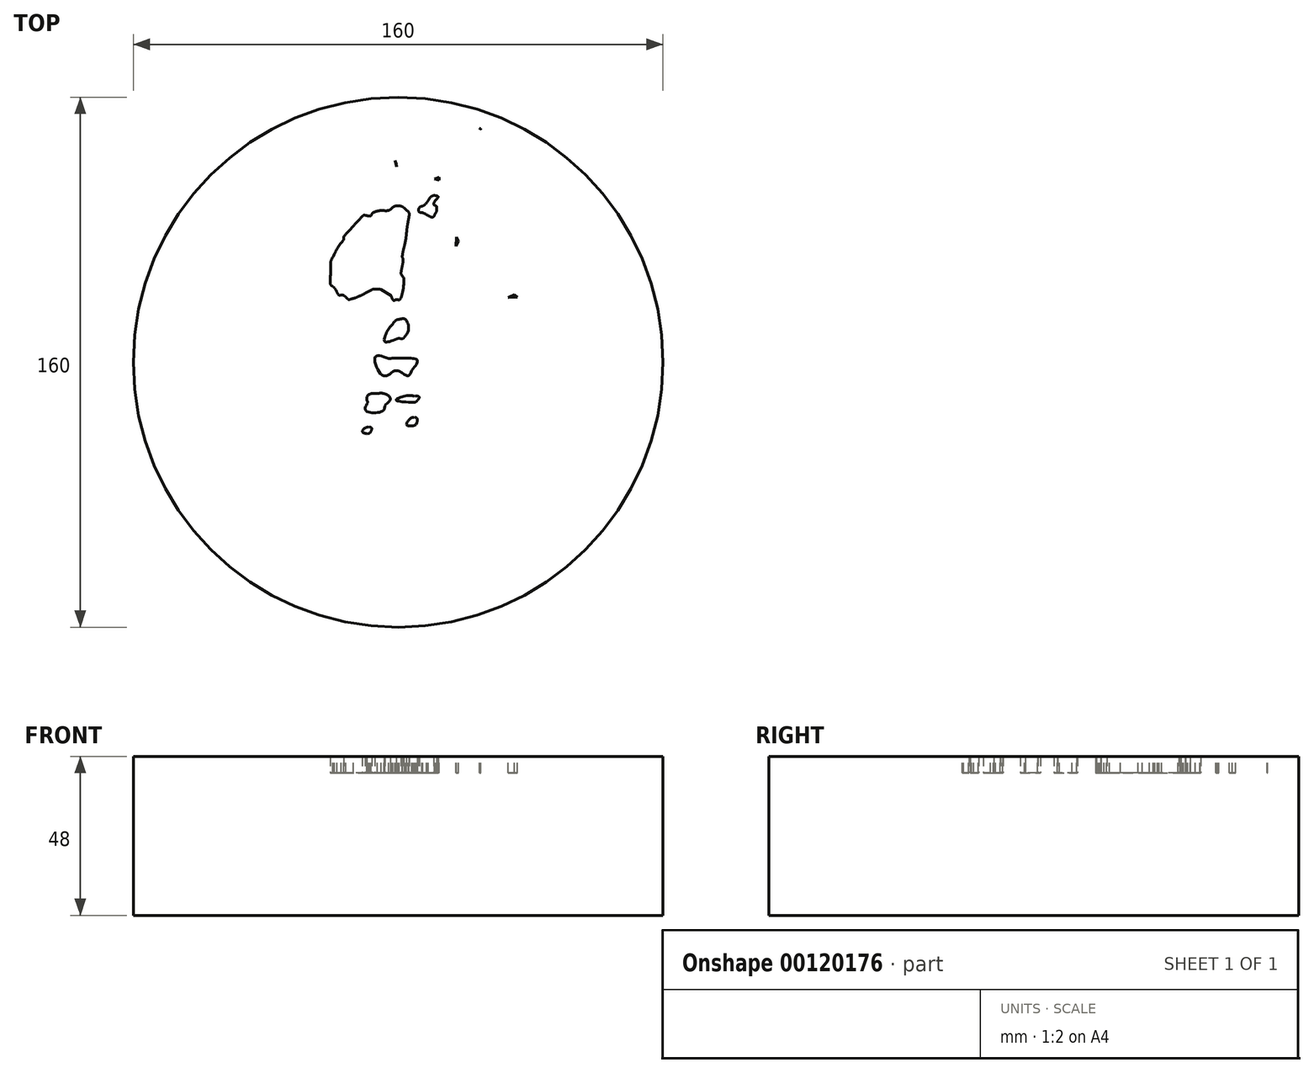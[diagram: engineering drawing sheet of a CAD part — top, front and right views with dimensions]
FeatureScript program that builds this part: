
annotation { "Feature Type Name" : "Feature", "Feature Type Description" : "" }
export const myFeature = defineFeature(function(context is Context, id is Id, definition is map)
    precondition{}
    {
        {
            var Q0;
            Q0=qCreatedBy(makeId("Top.planeOp"),FACE);
            var sketch = newSketch(context, id + "F0", { "sketchPlane" : qUnion([Q0])});
            skCircle(sketch, "E0", {"center": v(0, 0) * mm, "radius": 80 * mm});
            skSolve(sketch);
        }
        {
            var Q0;
            Q0 = qSketchRegion(id + "F0", true);
            extrude(context, id + "F1", {"entities" : qUnion([Q0]), "depth" : 48 * mm});
        }
        {
            var Q0;
            Q0=makeQuery(id+"F1.opExtrude","CAP_FACE",FACE,{"disambiguationData":[OSD([sQuery(id+"F0.wireOp",EDGE,"E0")])],"isStart":false});
            var sketch = newSketch(context, id + "F2", { "sketchPlane" : qUnion([Q0])});
            skFitSpline(sketch, "E1", {"points": [v(23.9, 70.72) * mm, v(23.7, 70.72) * mm, v(23.45, 70.7) * mm, v(22.97, 70.7) * mm]});
            skFitSpline(sketch, "E2", {"points": [v(22.97, 70.7) * mm, v(22.18, 70.72) * mm, v(21.25, 70.78) * mm, v(20.57, 70.38) * mm]});
            skFitSpline(sketch, "E3", {"points": [v(20.57, 70.38) * mm, v(19.9, 69.97) * mm, v(18.86, 69.22) * mm, v(18.86, 68.8) * mm]});
            skFitSpline(sketch, "E4", {"points": [v(18.86, 68.8) * mm, v(18.86, 68.69) * mm, v(19.34, 68.11) * mm, v(19.83, 67.45) * mm]});
            skFitSpline(sketch, "E5", {"points": [v(19.83, 67.45) * mm, v(21.5, 65.23) * mm, v(22.01, 64.9) * mm, v(22.41, 64.07) * mm]});
            skFitSpline(sketch, "E6", {"points": [v(22.41, 64.07) * mm, v(22.94, 63.51) * mm, v(22.84, 63.93) * mm, v(22.42, 62.97) * mm]});
            skFitSpline(sketch, "E7", {"points": [v(22.42, 62.97) * mm, v(22.16, 62.29) * mm, v(21.89, 62.17) * mm, v(20.75, 62.24) * mm]});
            skFitSpline(sketch, "E8", {"points": [v(20.75, 62.24) * mm, v(20, 62.28) * mm, v(19.03, 62.5) * mm, v(18.59, 62.74) * mm]});
            skFitSpline(sketch, "E9", {"points": [v(18.59, 62.74) * mm, v(18.1, 63) * mm, v(17.67, 63.03) * mm, v(17.5, 62.83) * mm]});
            skFitSpline(sketch, "E10", {"points": [v(17.5, 62.83) * mm, v(17.04, 62.33) * mm, v(16.38, 60.17) * mm, v(16.58, 59.85) * mm]});
            skFitSpline(sketch, "E11", {"points": [v(16.58, 59.85) * mm, v(16.68, 59.69) * mm, v(16.42, 59.45) * mm, v(16.02, 59.33) * mm]});
            skFitSpline(sketch, "E12", {"points": [v(16.02, 59.33) * mm, v(15.22, 59.07) * mm, v(12.6, 60.64) * mm, v(12.23, 61.6) * mm]});
            skFitSpline(sketch, "E13", {"points": [v(12.23, 61.6) * mm, v(11.95, 62.32) * mm, v(10.33, 63.72) * mm, v(9.75, 63.73) * mm]});
            skFitSpline(sketch, "E14", {"points": [v(9.75, 63.73) * mm, v(9.5, 63.74) * mm, v(7.43, 64.17) * mm, v(7.65, 64.94) * mm]});
            skFitSpline(sketch, "E15", {"points": [v(7.65, 64.94) * mm, v(8.28, 65.73) * mm, v(9.85, 64.96) * mm, v(10.98, 64.89) * mm]});
            skFitSpline(sketch, "E16", {"points": [v(10.98, 64.89) * mm, v(12.58, 64.79) * mm, v(13.07, 65.17) * mm, v(13.56, 66.88) * mm]});
            skFitSpline(sketch, "E17", {"points": [v(13.56, 66.88) * mm, v(13.92, 68.13) * mm, v(13.36, 68.64) * mm, v(11.8, 68.5) * mm]});
            skFitSpline(sketch, "E18", {"points": [v(11.8, 68.5) * mm, v(11.32, 68.47) * mm, v(10.85, 68.8) * mm, v(10.53, 68.98) * mm]});
            skFitSpline(sketch, "E19", {"points": [v(10.53, 68.98) * mm, v(9.88, 69.32) * mm, v(9.92, 69.46) * mm, v(8.6, 69.06) * mm]});
            skFitSpline(sketch, "E20", {"points": [v(8.6, 69.06) * mm, v(7.5, 68.74) * mm, v(7.03, 68.72) * mm, v(6.94, 69) * mm]});
            skFitSpline(sketch, "E21", {"points": [v(6.94, 69) * mm, v(6.87, 69.2) * mm, v(5.72, 69.1) * mm, v(4.97, 69.1) * mm]});
            skFitSpline(sketch, "E22", {"points": [v(4.97, 69.1) * mm, v(3.34, 69.1) * mm, v(1.85, 67.95) * mm, v(2.16, 66.99) * mm]});
            skFitSpline(sketch, "E23", {"points": [v(2.16, 66.99) * mm, v(2.64, 65.5) * mm, v(3.56, 64.36) * mm, v(3.7, 64.1) * mm]});
            skFitSpline(sketch, "E24", {"points": [v(4.06, 63.48) * mm, v(4.24, 63.16) * mm, v(4.67, 62.57) * mm, v(5.52, 62.15) * mm]});
            skFitSpline(sketch, "E25", {"points": [v(5.52, 62.15) * mm, v(7.27, 61.3) * mm, v(7.33, 60.85) * mm, v(5.77, 60.39) * mm]});
            skFitSpline(sketch, "E26", {"points": [v(5.77, 60.39) * mm, v(3.3, 59.66) * mm, v(3.12, 58.93) * mm, v(4.75, 56.28) * mm]});
            skFitSpline(sketch, "E27", {"points": [v(4.75, 56.28) * mm, v(5.33, 55.33) * mm, v(5.8, 54.32) * mm, v(5.8, 54.03) * mm]});
            skFitSpline(sketch, "E28", {"points": [v(5.8, 54.03) * mm, v(5.8, 53.21) * mm, v(4.89, 53.42) * mm, v(4.25, 54.4) * mm]});
            skFitSpline(sketch, "E29", {"points": [v(4.25, 54.4) * mm, v(3.74, 55.18) * mm, v(3.44, 55.27) * mm, v(1.4, 55.27) * mm]});
            skFitSpline(sketch, "E30", {"points": [v(1.4, 55.27) * mm, v(0.16, 55.27) * mm, v(-1.27, 55.09) * mm, v(-1.76, 54.86) * mm]});
            skFitSpline(sketch, "E31", {"points": [v(-1.76, 54.86) * mm, v(-3, 54.3) * mm, v(-3.3, 54.75) * mm, v(-2.36, 55.75) * mm]});
            skFitSpline(sketch, "E32", {"points": [v(-2.36, 55.75) * mm, v(-1.93, 56.2) * mm, v(-1.69, 57.02) * mm, v(-1.42, 57.4) * mm]});
            skFitSpline(sketch, "E33", {"points": [v(-1.42, 57.4) * mm, v(-1.03, 57.94) * mm, v(-0.47, 58.41) * mm, v(-0.48, 59.04) * mm]});
            skLineSegment(sketch, "E34", {"start": v(3.7, 64.1) * mm, "end": v(4.06, 63.48) * mm});
            skLineSegment(sketch, "E35", {"start": v(4.06, 63.48) * mm, "end": v(3.7, 64.1) * mm});
            skFitSpline(sketch, "E36", {"points": [v(-1, 60.95) * mm, v(-2, 61.77) * mm, v(-1.6, 62.77) * mm, v(-2.27, 63.24) * mm]});
            skFitSpline(sketch, "E37", {"points": [v(-2.27, 63.24) * mm, v(-3.1, 63.8) * mm, v(-5.09, 62.73) * mm, v(-5.28, 63) * mm]});
            skFitSpline(sketch, "E38", {"points": [v(-5.28, 63) * mm, v(-5.4, 63.19) * mm, v(-5.3, 63.47) * mm, v(-5.05, 63.63) * mm]});
            skFitSpline(sketch, "E39", {"points": [v(-5.05, 63.63) * mm, v(-4.48, 64) * mm, v(-3.87, 65.25) * mm, v(-3.32, 67.2) * mm]});
            skFitSpline(sketch, "E40", {"points": [v(-3.32, 67.2) * mm, v(-2.95, 68.5) * mm, v(-2.97, 68.8) * mm, v(-3.45, 69.27) * mm]});
            skFitSpline(sketch, "E41", {"points": [v(-3.45, 69.27) * mm, v(-3.76, 69.58) * mm, v(-4.38, 69.83) * mm, v(-4.83, 69.83) * mm]});
            skFitSpline(sketch, "E42", {"points": [v(-4.83, 69.83) * mm, v(-5.87, 69.83) * mm, v(-12.56, 66.55) * mm, v(-12.8, 65.93) * mm]});
            skFitSpline(sketch, "E43", {"points": [v(-12.8, 65.93) * mm, v(-13.1, 65.14) * mm, v(-11.77, 64.41) * mm, v(-10.33, 64.58) * mm]});
            skFitSpline(sketch, "E44", {"points": [v(-10.33, 64.58) * mm, v(-9.16, 64.71) * mm, v(-7.35, 64.9) * mm, v(-8.09, 64.19) * mm]});
            skFitSpline(sketch, "E45", {"points": [v(-8.09, 64.19) * mm, v(-8.45, 63.83) * mm, v(-10.77, 60.58) * mm, v(-10.77, 59.7) * mm]});
            skFitSpline(sketch, "E46", {"points": [v(-10.77, 59.7) * mm, v(-10.77, 58.63) * mm, v(-10.24, 58.3) * mm, v(-8.72, 58.4) * mm]});
            skFitSpline(sketch, "E47", {"points": [v(-8.72, 58.4) * mm, v(-7.83, 58.46) * mm, v(-6.58, 58.53) * mm, v(-5.65, 58.55) * mm]});
            skFitSpline(sketch, "E48", {"points": [v(-5.65, 58.55) * mm, v(-3.89, 58.59) * mm, v(-5.65, 57.2) * mm, v(-5.84, 56.66) * mm]});
            skLineSegment(sketch, "E49", {"start": v(-0.48, 59.04) * mm, "end": v(-0.5, 59.95) * mm});
            skLineSegment(sketch, "E50", {"start": v(-0.5, 59.95) * mm, "end": v(-1, 60.95) * mm});
            skLineSegment(sketch, "E51", {"start": v(-1, 60.95) * mm, "end": v(-0.48, 59.04) * mm});
            skFitSpline(sketch, "E52", {"points": [v(-6.67, 55.34) * mm, v(-7.13, 54.62) * mm, v(-7.75, 53.82) * mm, v(-8.06, 53.57) * mm]});
            skFitSpline(sketch, "E53", {"points": [v(-8.06, 53.57) * mm, v(-8.66, 53.07) * mm, v(-8.52, 52.3) * mm, v(-7.66, 51.3) * mm]});
            skFitSpline(sketch, "E54", {"points": [v(-7.66, 51.3) * mm, v(-7.2, 50.77) * mm, v(-6.78, 50.7) * mm, v(-5.06, 50.9) * mm]});
            skFitSpline(sketch, "E55", {"points": [v(-5.06, 50.9) * mm, v(-2.63, 51.18) * mm, v(-2.44, 50.8) * mm, v(-4.3, 49.4) * mm]});
            skFitSpline(sketch, "E56", {"points": [v(-4.3, 49.4) * mm, v(-5.28, 48.64) * mm, v(-6, 48.4) * mm, v(-7.43, 48.36) * mm]});
            skFitSpline(sketch, "E57", {"points": [v(-7.43, 48.36) * mm, v(-9.27, 48.3) * mm, v(-10.48, 47.64) * mm, v(-13.86, 44.82) * mm]});
            skFitSpline(sketch, "E58", {"points": [v(-13.86, 44.82) * mm, v(-14.3, 44.46) * mm, v(-15.36, 43.6) * mm, v(-16.24, 42.93) * mm]});
            skFitSpline(sketch, "E59", {"points": [v(-16.24, 42.93) * mm, v(-17.11, 42.25) * mm, v(-17.83, 41.52) * mm, v(-17.83, 41.3) * mm]});
            skFitSpline(sketch, "E60", {"points": [v(-17.83, 41.3) * mm, v(-17.83, 41.09) * mm, v(-18.36, 40.21) * mm, v(-19.01, 39.36) * mm]});
            skFitSpline(sketch, "E61", {"points": [v(-19.01, 39.36) * mm, v(-20.45, 37.47) * mm, v(-21.54, 35.38) * mm, v(-21.87, 33.85) * mm]});
            skFitSpline(sketch, "E62", {"points": [v(-21.87, 33.85) * mm, v(-22, 33.22) * mm, v(-22.26, 32.61) * mm, v(-22.44, 32.5) * mm]});
            skFitSpline(sketch, "E63", {"points": [v(-22.44, 32.5) * mm, v(-22.62, 32.4) * mm, v(-22.77, 31.99) * mm, v(-22.77, 31.6) * mm]});
            skFitSpline(sketch, "E64", {"points": [v(-22.77, 31.6) * mm, v(-22.77, 31.21) * mm, v(-23, 30.44) * mm, v(-23.29, 29.89) * mm]});
            skFitSpline(sketch, "E65", {"points": [v(-23.29, 29.89) * mm, v(-24.54, 27.46) * mm, v(-24.12, 23.5) * mm, v(-22.3, 20.61) * mm]});
            skFitSpline(sketch, "E66", {"points": [v(-22.3, 20.61) * mm, v(-21.71, 19.7) * mm, v(-21.13, 18.94) * mm, v(-21, 18.94) * mm]});
            skFitSpline(sketch, "E67", {"points": [v(-21, 18.94) * mm, v(-20.88, 18.94) * mm, v(-20.24, 18.46) * mm, v(-19.6, 17.88) * mm]});
            skFitSpline(sketch, "E68", {"points": [v(-19.6, 17.88) * mm, v(-18.94, 17.3) * mm, v(-18.13, 16.82) * mm, v(-17.79, 16.82) * mm]});
            skFitSpline(sketch, "E69", {"points": [v(-17.79, 16.82) * mm, v(-17.44, 16.82) * mm, v(-17.07, 16.66) * mm, v(-16.95, 16.47) * mm]});
            skFitSpline(sketch, "E70", {"points": [v(-16.95, 16.47) * mm, v(-16.65, 15.99) * mm, v(-11.23, 16.01) * mm, v(-10.93, 16.5) * mm]});
            skFitSpline(sketch, "E71", {"points": [v(-10.93, 16.5) * mm, v(-10.8, 16.7) * mm, v(-9.85, 17.42) * mm, v(-8.8, 18.09) * mm]});
            skFitSpline(sketch, "E72", {"points": [v(-8.8, 18.09) * mm, v(-5.96, 19.9) * mm, v(-5.07, 19.66) * mm, v(-6.05, 17.3) * mm]});
            skFitSpline(sketch, "E73", {"points": [v(-6.05, 17.3) * mm, v(-6.57, 16.05) * mm, v(-6.57, 15.88) * mm, v(-6, 14.8) * mm]});
            skLineSegment(sketch, "E74", {"start": v(-5.84, 56.66) * mm, "end": v(-6.67, 55.34) * mm});
            skLineSegment(sketch, "E75", {"start": v(-6.67, 55.34) * mm, "end": v(-5.84, 56.66) * mm});
            skFitSpline(sketch, "E76", {"points": [v(-5.39, 13.68) * mm, v(-5.28, 12.38) * mm, v(-4.98, 11.39) * mm, v(-5.3, 10.44) * mm]});
            skFitSpline(sketch, "E77", {"points": [v(-5.3, 10.44) * mm, v(-4.92, 6.56) * mm, v(-6.78, 3.05) * mm, v(-8.22, -0.42) * mm]});
            skFitSpline(sketch, "E78", {"points": [v(-8.22, -0.42) * mm, v(-9.52, -3.6) * mm, v(-10.26, -7.02) * mm, v(-11.35, -10.21) * mm]});
            skFitSpline(sketch, "E79", {"points": [v(-11.35, -10.21) * mm, v(-11.76, -13.4) * mm, v(-12.5, -16.53) * mm, v(-13.6, -19.56) * mm]});
            skFitSpline(sketch, "E80", {"points": [v(-13.6, -19.56) * mm, v(-12.29, -22.65) * mm, v(-10.4, -25.55) * mm, v(-9.64, -28.84) * mm]});
            skFitSpline(sketch, "E81", {"points": [v(-9.64, -28.84) * mm, v(-9.6, -32.33) * mm, v(-8.56, -35.7) * mm, v(-8.66, -39.2) * mm]});
            skFitSpline(sketch, "E82", {"points": [v(-8.66, -39.2) * mm, v(-7.14, -45.43) * mm, v(-7.6, -51.93) * mm, v(-7.18, -58.3) * mm]});
            skFitSpline(sketch, "E83", {"points": [v(-7.18, -58.3) * mm, v(-6.55, -63.17) * mm, v(-12.4, -62.24) * mm, v(-15.18, -63.73) * mm]});
            skFitSpline(sketch, "E84", {"points": [v(-15.18, -63.73) * mm, v(-18.35, -65.08) * mm, v(-21.94, -64.68) * mm, v(-24.8, -61.78) * mm]});
            skFitSpline(sketch, "E85", {"points": [v(-24.8, -61.78) * mm, v(-26.69, -59.87) * mm, v(-27.55, -62.67) * mm, v(-26.8, -64.28) * mm]});
            skFitSpline(sketch, "E86", {"points": [v(-26.8, -64.28) * mm, v(-27.92, -64.34) * mm, v(-29.65, -63.82) * mm, v(-30.85, -64.1) * mm]});
            skFitSpline(sketch, "E87", {"points": [v(-30.85, -64.1) * mm, v(-30.95, -65.2) * mm, v(-29.3, -65.92) * mm, v(-28.86, -66.78) * mm]});
            skFitSpline(sketch, "E88", {"points": [v(-28.86, -66.78) * mm, v(-29.51, -67.36) * mm, v(-31.13, -68.2) * mm, v(-31.03, -69) * mm]});
            skFitSpline(sketch, "E89", {"points": [v(-31.03, -69) * mm, v(-30.94, -69.63) * mm, v(-29.69, -70.08) * mm, v(-28.88, -70.48) * mm]});
            skFitSpline(sketch, "E90", {"points": [v(-28.88, -70.48) * mm, v(-27.89, -70.98) * mm, v(-24.25, -70.62) * mm, v(-20.84, -70.23) * mm]});
            skFitSpline(sketch, "E91", {"points": [v(-20.84, -70.23) * mm, v(-17.2, -69.82) * mm, v(-14.59, -70.82) * mm, v(-11.19, -68.77) * mm]});
            skFitSpline(sketch, "E92", {"points": [v(-11.19, -68.77) * mm, v(-8.34, -67.05) * mm, v(-3.3, -67.46) * mm, v(-2.78, -63.46) * mm]});
            skFitSpline(sketch, "E93", {"points": [v(-2.78, -63.46) * mm, v(-3.8, -60.02) * mm, v(-3.69, -56.22) * mm, v(-5.35, -53) * mm]});
            skFitSpline(sketch, "E94", {"points": [v(-5.35, -53) * mm, v(-4.77, -48.66) * mm, v(-4.45, -44.23) * mm, v(-5.27, -39.9) * mm]});
            skFitSpline(sketch, "E95", {"points": [v(-5.27, -39.9) * mm, v(-7.08, -35.92) * mm, v(-6.64, -31.42) * mm, v(-7.08, -27.18) * mm]});
            skFitSpline(sketch, "E96", {"points": [v(-7.08, -27.18) * mm, v(-7.08, -25.87) * mm, v(-7.81, -24.34) * mm, v(-6.5, -23.44) * mm]});
            skFitSpline(sketch, "E97", {"points": [v(-6.5, -23.44) * mm, v(-3.66, -21.44) * mm, v(-4.72, -17.07) * mm, v(-1.7, -15.5) * mm]});
            skFitSpline(sketch, "E98", {"points": [v(-1.7, -15.5) * mm, v(0.75, -17.58) * mm, v(2.51, -20.76) * mm, v(4.99, -23.1) * mm]});
            skFitSpline(sketch, "E99", {"points": [v(4.99, -23.1) * mm, v(4.47, -25.89) * mm, v(7.27, -27.84) * mm, v(6.25, -30.43) * mm]});
            skFitSpline(sketch, "E100", {"points": [v(6.25, -30.43) * mm, v(7.8, -34.18) * mm, v(6.08, -38.12) * mm, v(6.86, -42.05) * mm]});
            skFitSpline(sketch, "E101", {"points": [v(6.86, -42.05) * mm, v(7.27, -46.6) * mm, v(5.98, -50.97) * mm, v(5.68, -55.46) * mm]});
            skFitSpline(sketch, "E102", {"points": [v(5.68, -55.46) * mm, v(5.45, -58.85) * mm, v(3.24, -62.46) * mm, v(4.27, -65.72) * mm]});
            skFitSpline(sketch, "E103", {"points": [v(4.27, -65.72) * mm, v(6.32, -67.7) * mm, v(9.07, -65.7) * mm, v(11.1, -64.67) * mm]});
            skFitSpline(sketch, "E104", {"points": [v(11.1, -64.67) * mm, v(14.3, -62.4) * mm, v(20.28, -57.24) * mm, v(22.6, -54.28) * mm]});
            skFitSpline(sketch, "E105", {"points": [v(22.6, -54.28) * mm, v(29.36, -52.5) * mm, v(26.52, -53.64) * mm, v(29.36, -52.5) * mm]});
            skFitSpline(sketch, "E106", {"points": [v(29.36, -52.5) * mm, v(31.77, -51.53) * mm, v(32.61, -50.24) * mm, v(31.42, -49.6) * mm]});
            skFitSpline(sketch, "E107", {"points": [v(31.42, -49.6) * mm, v(30.25, -48.96) * mm, v(27.26, -49.63) * mm, v(25.78, -49.23) * mm]});
            skFitSpline(sketch, "E108", {"points": [v(25.78, -49.23) * mm, v(27.4, -46.88) * mm, v(32.18, -45.66) * mm, v(30.39, -43.4) * mm]});
            skFitSpline(sketch, "E109", {"points": [v(30.39, -43.4) * mm, v(28.58, -41.11) * mm, v(25.64, -44.47) * mm, v(24.21, -45.43) * mm]});
            skFitSpline(sketch, "E110", {"points": [v(24.21, -45.43) * mm, v(24.1, -44.26) * mm, v(25.21, -41.72) * mm, v(23.4, -41.66) * mm]});
            skFitSpline(sketch, "E111", {"points": [v(23.4, -41.66) * mm, v(21.66, -41.6) * mm, v(21.36, -47.49) * mm, v(20.5, -49.07) * mm]});
            skFitSpline(sketch, "E112", {"points": [v(20.5, -49.07) * mm, v(17.43, -51.02) * mm, v(15.19, -54.1) * mm, v(12.84, -56.9) * mm]});
            skFitSpline(sketch, "E113", {"points": [v(12.84, -56.9) * mm, v(11.7, -58.88) * mm, v(6.15, -61.65) * mm, v(8.2, -57.15) * mm]});
            skFitSpline(sketch, "E114", {"points": [v(8.2, -57.15) * mm, v(8.86, -52.68) * mm, v(9.03, -48.15) * mm, v(9.53, -43.66) * mm]});
            skFitSpline(sketch, "E115", {"points": [v(9.53, -43.66) * mm, v(9.75, -40.72) * mm, v(9.42, -37.42) * mm, v(8.73, -34.52) * mm]});
            skFitSpline(sketch, "E116", {"points": [v(8.73, -34.52) * mm, v(9.58, -30.47) * mm, v(7.29, -26.7) * mm, v(7.64, -22.7) * mm]});
            skFitSpline(sketch, "E117", {"points": [v(7.64, -22.7) * mm, v(8.74, -18.06) * mm, v(8.9, -13.27) * mm, v(8.49, -8.54) * mm]});
            skFitSpline(sketch, "E118", {"points": [v(8.49, -8.54) * mm, v(8.26, -4.97) * mm, v(6.72, -1.71) * mm, v(6.23, 1.72) * mm]});
            skFitSpline(sketch, "E119", {"points": [v(6.23, 1.72) * mm, v(5.36, 5.56) * mm, v(4.63, 9.9) * mm, v(3.43, 13.67) * mm]});
            skLineSegment(sketch, "E120", {"start": v(-6, 14.8) * mm, "end": v(-5.39, 13.68) * mm});
            skLineSegment(sketch, "E121", {"start": v(-5.39, 13.68) * mm, "end": v(-6, 14.8) * mm});
            skFitSpline(sketch, "E122", {"points": [v(3.2, 15.38) * mm, v(3.07, 16.36) * mm, v(3.11, 17.21) * mm, v(3.3, 17.33) * mm]});
            skFitSpline(sketch, "E123", {"points": [v(3.3, 17.33) * mm, v(3.48, 17.44) * mm, v(3.62, 18.68) * mm, v(3.61, 20.09) * mm]});
            skFitSpline(sketch, "E124", {"points": [v(3.61, 20.09) * mm, v(3.6, 21.5) * mm, v(3.71, 23.83) * mm, v(3.86, 25.29) * mm]});
            skFitSpline(sketch, "E125", {"points": [v(3.86, 25.29) * mm, v(4, 26.74) * mm, v(4.17, 28.65) * mm, v(4.23, 29.52) * mm]});
            skFitSpline(sketch, "E126", {"points": [v(4.23, 29.52) * mm, v(4.38, 31.69) * mm, v(4.62, 32.94) * mm, v(5.11, 34.13) * mm]});
            skFitSpline(sketch, "E127", {"points": [v(5.11, 34.13) * mm, v(5.34, 34.69) * mm, v(5.55, 35.9) * mm, v(5.58, 36.83) * mm]});
            skFitSpline(sketch, "E128", {"points": [v(5.58, 36.83) * mm, v(5.63, 38.4) * mm, v(5.7, 38.51) * mm, v(6.51, 38.43) * mm]});
            skFitSpline(sketch, "E129", {"points": [v(6.51, 38.43) * mm, v(7, 38.39) * mm, v(8.39, 38.3) * mm, v(9.6, 38.24) * mm]});
            skFitSpline(sketch, "E130", {"points": [v(9.6, 38.24) * mm, v(10.82, 38.17) * mm, v(12, 37.93) * mm, v(12.23, 37.7) * mm]});
            skFitSpline(sketch, "E131", {"points": [v(12.23, 37.7) * mm, v(12.46, 37.47) * mm, v(13.08, 37.28) * mm, v(13.6, 37.28) * mm]});
            skFitSpline(sketch, "E132", {"points": [v(13.6, 37.28) * mm, v(15.14, 37.28) * mm, v(15.43, 35.66) * mm, v(14.28, 33.4) * mm]});
            skFitSpline(sketch, "E133", {"points": [v(14.28, 33.4) * mm, v(13.48, 31.84) * mm, v(13.35, 30.01) * mm, v(14.01, 29.78) * mm]});
            skFitSpline(sketch, "E134", {"points": [v(14.01, 29.78) * mm, v(14.25, 29.7) * mm, v(15.42, 29.7) * mm, v(16.6, 29.8) * mm]});
            skFitSpline(sketch, "E135", {"points": [v(16.6, 29.8) * mm, v(18.93, 29.98) * mm, v(19.5, 29.66) * mm, v(18.88, 28.5) * mm]});
            skFitSpline(sketch, "E136", {"points": [v(18.88, 28.5) * mm, v(18.68, 28.13) * mm, v(18.42, 26.72) * mm, v(18.3, 25.38) * mm]});
            skFitSpline(sketch, "E137", {"points": [v(18.3, 25.38) * mm, v(18.1, 23.38) * mm, v(18.18, 22.76) * mm, v(18.68, 22) * mm]});
            skFitSpline(sketch, "E138", {"points": [v(18.68, 22) * mm, v(19.45, 20.82) * mm, v(20.16, 20.82) * mm, v(22.6, 21.96) * mm]});
            skFitSpline(sketch, "E139", {"points": [v(22.6, 21.96) * mm, v(24, 22.63) * mm, v(24.8, 22.8) * mm, v(25.6, 22.64) * mm]});
            skFitSpline(sketch, "E140", {"points": [v(25.6, 22.64) * mm, v(26.76, 22.38) * mm, v(27.43, 21.24) * mm, v(26.96, 20.33) * mm]});
            skFitSpline(sketch, "E141", {"points": [v(26.96, 20.33) * mm, v(26.5, 19.47) * mm, v(26.82, 17.8) * mm, v(27.54, 17.28) * mm]});
            skFitSpline(sketch, "E142", {"points": [v(27.54, 17.28) * mm, v(28.01, 16.93) * mm, v(29.06, 16.86) * mm, v(31.6, 17) * mm]});
            skFitSpline(sketch, "E143", {"points": [v(31.6, 17) * mm, v(34.44, 17.15) * mm, v(35.04, 17.1) * mm, v(35.21, 16.65) * mm]});
            skFitSpline(sketch, "E144", {"points": [v(35.21, 16.65) * mm, v(35.33, 16.36) * mm, v(35.74, 16.12) * mm, v(36.14, 16.12) * mm]});
            skFitSpline(sketch, "E145", {"points": [v(36.14, 16.12) * mm, v(37.25, 16.12) * mm, v(37.14, 18.54) * mm, v(35.98, 19.63) * mm]});
            skLineSegment(sketch, "E146", {"start": v(3.43, 13.67) * mm, "end": v(3.2, 15.38) * mm});
            skLineSegment(sketch, "E147", {"start": v(3.2, 15.38) * mm, "end": v(3.43, 13.67) * mm});
            skFitSpline(sketch, "E148", {"points": [v(33.22, 19.52) * mm, v(31.18, 18.52) * mm, v(29.99, 18.34) * mm, v(29.6, 18.98) * mm]});
            skFitSpline(sketch, "E149", {"points": [v(29.6, 18.98) * mm, v(29.46, 19.2) * mm, v(29.31, 20.35) * mm, v(29.26, 21.54) * mm]});
            skFitSpline(sketch, "E150", {"points": [v(29.26, 21.54) * mm, v(29.09, 25.98) * mm, v(28.18, 26.74) * mm, v(24.79, 25.3) * mm]});
            skFitSpline(sketch, "E151", {"points": [v(24.79, 25.3) * mm, v(23.5, 24.77) * mm, v(22.09, 24.34) * mm, v(21.63, 24.36) * mm]});
            skFitSpline(sketch, "E152", {"points": [v(21.63, 24.36) * mm, v(20.89, 24.4) * mm, v(20.83, 24.54) * mm, v(20.93, 26) * mm]});
            skFitSpline(sketch, "E153", {"points": [v(20.93, 26) * mm, v(21, 26.87) * mm, v(21.27, 28.12) * mm, v(21.54, 28.77) * mm]});
            skFitSpline(sketch, "E154", {"points": [v(21.54, 28.77) * mm, v(22.24, 30.45) * mm, v(22.16, 31.11) * mm, v(21.15, 32.2) * mm]});
            skFitSpline(sketch, "E155", {"points": [v(21.15, 32.2) * mm, v(20.33, 33.09) * mm, v(20.16, 33.13) * mm, v(19, 32.78) * mm]});
            skFitSpline(sketch, "E156", {"points": [v(19, 32.78) * mm, v(17.73, 32.39) * mm, v(16.74, 32.52) * mm, v(16.74, 33.08) * mm]});
            skFitSpline(sketch, "E157", {"points": [v(16.74, 33.08) * mm, v(16.74, 33.25) * mm, v(17.09, 34.09) * mm, v(17.5, 34.94) * mm]});
            skLineSegment(sketch, "E158", {"start": v(35.98, 19.63) * mm, "end": v(35.12, 20.45) * mm});
            skLineSegment(sketch, "E159", {"start": v(35.12, 20.45) * mm, "end": v(33.22, 19.52) * mm});
            skLineSegment(sketch, "E160", {"start": v(33.22, 19.52) * mm, "end": v(35.98, 19.63) * mm});
            skFitSpline(sketch, "E161", {"points": [v(17.56, 37.86) * mm, v(17.1, 38.77) * mm, v(16.57, 39.26) * mm, v(16, 39.34) * mm]});
            skFitSpline(sketch, "E162", {"points": [v(16, 39.34) * mm, v(14.96, 39.5) * mm, v(14.28, 40.03) * mm, v(14.28, 40.7) * mm]});
            skFitSpline(sketch, "E163", {"points": [v(14.28, 40.7) * mm, v(14.28, 41.4) * mm, v(17.68, 45.41) * mm, v(19.12, 46.4) * mm]});
            skFitSpline(sketch, "E164", {"points": [v(19.12, 46.4) * mm, v(20.24, 47.17) * mm, v(21.63, 47.22) * mm, v(21.17, 46.48) * mm]});
            skFitSpline(sketch, "E165", {"points": [v(21.17, 46.48) * mm, v(21.05, 46.3) * mm, v(20.8, 45.25) * mm, v(20.6, 44.15) * mm]});
            skFitSpline(sketch, "E166", {"points": [v(20.6, 44.15) * mm, v(20.27, 42.42) * mm, v(20.3, 42.06) * mm, v(20.84, 41.48) * mm]});
            skFitSpline(sketch, "E167", {"points": [v(20.84, 41.48) * mm, v(21.6, 40.63) * mm, v(22.08, 40.78) * mm, v(25.04, 42.77) * mm]});
            skFitSpline(sketch, "E168", {"points": [v(25.04, 42.77) * mm, v(26.33, 43.63) * mm, v(27.58, 44.34) * mm, v(27.81, 44.34) * mm]});
            skFitSpline(sketch, "E169", {"points": [v(27.81, 44.34) * mm, v(28.6, 44.34) * mm, v(29.1, 43.5) * mm, v(29.1, 42.15) * mm]});
            skFitSpline(sketch, "E170", {"points": [v(29.1, 42.15) * mm, v(29.1, 39.53) * mm, v(31.57, 38.56) * mm, v(34.04, 40.23) * mm]});
            skFitSpline(sketch, "E171", {"points": [v(34.04, 40.23) * mm, v(36.35, 41.78) * mm, v(38.99, 42.95) * mm, v(39.14, 42.48) * mm]});
            skFitSpline(sketch, "E172", {"points": [v(39.14, 42.48) * mm, v(39.22, 42.24) * mm, v(39.7, 40.77) * mm, v(40.21, 39.22) * mm]});
            skFitSpline(sketch, "E173", {"points": [v(40.21, 39.22) * mm, v(41.54, 35.18) * mm, v(42.44, 34.4) * mm, v(44.17, 35.85) * mm]});
            skFitSpline(sketch, "E174", {"points": [v(44.17, 35.85) * mm, v(45.15, 36.67) * mm, v(45.18, 37.4) * mm, v(44.26, 38.03) * mm]});
            skFitSpline(sketch, "E175", {"points": [v(44.26, 38.03) * mm, v(43.68, 38.43) * mm, v(43.52, 39.07) * mm, v(43.33, 41.61) * mm]});
            skFitSpline(sketch, "E176", {"points": [v(43.33, 41.61) * mm, v(43.07, 45.08) * mm, v(42.5, 46.11) * mm, v(40.76, 46.31) * mm]});
            skFitSpline(sketch, "E177", {"points": [v(40.76, 46.31) * mm, v(39.71, 46.44) * mm, v(36.72, 45.33) * mm, v(36.3, 44.67) * mm]});
            skFitSpline(sketch, "E178", {"points": [v(36.3, 44.67) * mm, v(35.98, 44.14) * mm, v(33.52, 42.65) * mm, v(32.76, 42.51) * mm]});
            skFitSpline(sketch, "E179", {"points": [v(32.76, 42.51) * mm, v(32.2, 42.42) * mm, v(32.11, 42.59) * mm, v(32.2, 43.54) * mm]});
            skFitSpline(sketch, "E180", {"points": [v(32.2, 43.54) * mm, v(32.27, 44.16) * mm, v(32.19, 44.88) * mm, v(32.03, 45.12) * mm]});
            skFitSpline(sketch, "E181", {"points": [v(32.03, 45.12) * mm, v(31.87, 45.37) * mm, v(31.74, 46.29) * mm, v(31.74, 47.16) * mm]});
            skFitSpline(sketch, "E182", {"points": [v(31.74, 47.16) * mm, v(31.74, 48.64) * mm, v(31.67, 48.76) * mm, v(30.75, 48.86) * mm]});
            skFitSpline(sketch, "E183", {"points": [v(30.75, 48.86) * mm, v(30.17, 48.93) * mm, v(29.02, 48.6) * mm, v(28.01, 48.06) * mm]});
            skFitSpline(sketch, "E184", {"points": [v(28.01, 48.06) * mm, v(27.05, 47.56) * mm, v(26.27, 47.25) * mm, v(26.27, 47.38) * mm]});
            skFitSpline(sketch, "E185", {"points": [v(26.27, 47.38) * mm, v(26.27, 47.5) * mm, v(26.06, 47.43) * mm, v(25.8, 47.22) * mm]});
            skFitSpline(sketch, "E186", {"points": [v(25.8, 47.22) * mm, v(25.46, 46.93) * mm, v(25.2, 47.07) * mm, v(24.76, 47.83) * mm]});
            skFitSpline(sketch, "E187", {"points": [v(24.76, 47.83) * mm, v(24.44, 48.38) * mm, v(24.25, 48.9) * mm, v(24.35, 49) * mm]});
            skFitSpline(sketch, "E188", {"points": [v(24.35, 49) * mm, v(24.45, 49.1) * mm, v(24.37, 49.87) * mm, v(24.19, 50.72) * mm]});
            skFitSpline(sketch, "E189", {"points": [v(24.19, 50.72) * mm, v(23.95, 51.78) * mm, v(23.96, 52.4) * mm, v(24.22, 52.71) * mm]});
            skFitSpline(sketch, "E190", {"points": [v(24.22, 52.71) * mm, v(24.85, 53.47) * mm, v(24.4, 53.5) * mm, v(22.9, 52.83) * mm]});
            skFitSpline(sketch, "E191", {"points": [v(22.9, 52.83) * mm, v(22.11, 52.48) * mm, v(21.2, 51.78) * mm, v(20.87, 51.27) * mm]});
            skFitSpline(sketch, "E192", {"points": [v(20.87, 51.27) * mm, v(20.53, 50.75) * mm, v(20.06, 50.33) * mm, v(19.82, 50.33) * mm]});
            skFitSpline(sketch, "E193", {"points": [v(19.82, 50.33) * mm, v(19.43, 50.33) * mm, v(17.44, 48.28) * mm, v(16.27, 46.66) * mm]});
            skFitSpline(sketch, "E194", {"points": [v(16.27, 46.66) * mm, v(16, 46.29) * mm, v(15.56, 46.08) * mm, v(15.27, 46.19) * mm]});
            skFitSpline(sketch, "E195", {"points": [v(15.27, 46.19) * mm, v(14.85, 46.35) * mm, v(14.8, 46.77) * mm, v(15, 48.27) * mm]});
            skFitSpline(sketch, "E196", {"points": [v(15, 48.27) * mm, v(15.3, 50.48) * mm, v(14.84, 53.86) * mm, v(14.2, 54.28) * mm]});
            skFitSpline(sketch, "E197", {"points": [v(14.2, 54.28) * mm, v(13.95, 54.44) * mm, v(13.11, 54.75) * mm, v(12.33, 54.97) * mm]});
            skLineSegment(sketch, "E198", {"start": v(17.5, 34.94) * mm, "end": v(18.26, 36.5) * mm});
            skLineSegment(sketch, "E199", {"start": v(18.26, 36.5) * mm, "end": v(17.56, 37.86) * mm});
            skLineSegment(sketch, "E200", {"start": v(17.56, 37.86) * mm, "end": v(17.5, 34.94) * mm});
            skFitSpline(sketch, "E201", {"points": [v(12.33, 55.86) * mm, v(13.3, 56.21) * mm, v(14.3, 56.29) * mm, v(15.5, 56.1) * mm]});
            skFitSpline(sketch, "E202", {"points": [v(15.5, 56.1) * mm, v(18.02, 55.74) * mm, v(20.56, 55.93) * mm, v(21.83, 56.58) * mm]});
            skFitSpline(sketch, "E203", {"points": [v(21.83, 56.58) * mm, v(22.98, 57.16) * mm, v(23.39, 57.67) * mm, v(23.97, 59.21) * mm]});
            skFitSpline(sketch, "E204", {"points": [v(23.97, 59.21) * mm, v(24.17, 59.73) * mm, v(25.04, 60.7) * mm, v(25.92, 61.35) * mm]});
            skFitSpline(sketch, "E205", {"points": [v(25.92, 61.35) * mm, v(26.84, 62.04) * mm, v(27.55, 62.88) * mm, v(27.62, 63.36) * mm]});
            skFitSpline(sketch, "E206", {"points": [v(27.62, 63.36) * mm, v(27.03, 64.38) * mm, v(26.58, 65.21) * mm, v(25.77, 66.43) * mm]});
            skFitSpline(sketch, "E207", {"points": [v(25.77, 66.43) * mm, v(25.44, 67.3) * mm, v(26.13, 67.88) * mm, v(26.93, 67.38) * mm]});
            skFitSpline(sketch, "E208", {"points": [v(26.93, 67.38) * mm, v(27.46, 67.05) * mm, v(27.65, 67.13) * mm, v(28.1, 67.92) * mm]});
            skFitSpline(sketch, "E209", {"points": [v(28.1, 67.92) * mm, v(28.7, 68.94) * mm, v(28.52, 69.85) * mm, v(27.68, 70.03) * mm]});
            skFitSpline(sketch, "E210", {"points": [v(27.68, 70.03) * mm, v(26.91, 70.18) * mm, v(27.07, 70.14) * mm, v(25.84, 70.46) * mm]});
            skFitSpline(sketch, "E211", {"points": [v(25.84, 70.46) * mm, v(24.52, 70.6) * mm, v(24.97, 70.43) * mm, v(24.52, 70.6) * mm]});
            skFitSpline(sketch, "E212", {"points": [v(24.52, 70.6) * mm, v(24.23, 70.7) * mm, v(24.09, 70.72) * mm, v(23.9, 70.72) * mm]});
            skLineSegment(sketch, "E213", {"start": v(12.33, 54.97) * mm, "end": v(10.92, 55.36) * mm});
            skLineSegment(sketch, "E214", {"start": v(10.92, 55.36) * mm, "end": v(12.33, 55.86) * mm});
            skLineSegment(sketch, "E215", {"start": v(12.33, 55.86) * mm, "end": v(12.33, 54.97) * mm});
            skFitSpline(sketch, "E216", {"points": [v(11.4, 50.27) * mm, v(11.56, 50.26) * mm, v(11.71, 50.22) * mm, v(11.84, 50.13) * mm]});
            skFitSpline(sketch, "E217", {"points": [v(11.84, 50.13) * mm, v(12.07, 50) * mm, v(12.03, 49.7) * mm, v(11.7, 49.33) * mm]});
            skFitSpline(sketch, "E218", {"points": [v(11.7, 49.33) * mm, v(11, 48.5) * mm, v(10.72, 47.57) * mm, v(11.12, 47.33) * mm]});
            skFitSpline(sketch, "E219", {"points": [v(11.12, 47.33) * mm, v(11.56, 47.05) * mm, v(11.55, 45.52) * mm, v(11.09, 44.67) * mm]});
            skFitSpline(sketch, "E220", {"points": [v(11.09, 44.67) * mm, v(10.67, 43.89) * mm, v(9.9, 43.84) * mm, v(8.63, 44.53) * mm]});
            skFitSpline(sketch, "E221", {"points": [v(8.63, 44.53) * mm, v(8.15, 44.8) * mm, v(7.47, 45.09) * mm, v(7.13, 45.19) * mm]});
            skFitSpline(sketch, "E222", {"points": [v(7.13, 45.19) * mm, v(6.23, 45.46) * mm, v(6.38, 46.62) * mm, v(7.39, 47.16) * mm]});
            skFitSpline(sketch, "E223", {"points": [v(7.39, 47.16) * mm, v(7.87, 47.41) * mm, v(8.62, 48.15) * mm, v(9.06, 48.79) * mm]});
            skFitSpline(sketch, "E224", {"points": [v(9.06, 48.79) * mm, v(9.7, 49.72) * mm, v(10.68, 50.31) * mm, v(11.4, 50.27) * mm]});
            skFitSpline(sketch, "E225", {"points": [v(-0.16, 47.16) * mm, v(0.66, 47.17) * mm, v(1.52, 46.81) * mm, v(2.29, 46.1) * mm]});
            skFitSpline(sketch, "E226", {"points": [v(2.29, 46.1) * mm, v(3.34, 45.11) * mm, v(3.4, 44.91) * mm, v(3.18, 43.54) * mm]});
            skFitSpline(sketch, "E227", {"points": [v(3.18, 43.54) * mm, v(2.77, 41.07) * mm, v(2.67, 40.36) * mm, v(2.48, 38.61) * mm]});
            skFitSpline(sketch, "E228", {"points": [v(2.48, 38.61) * mm, v(2.37, 37.7) * mm, v(2.04, 35.82) * mm, v(1.73, 34.45) * mm]});
            skFitSpline(sketch, "E229", {"points": [v(1.73, 34.45) * mm, v(1.41, 33.08) * mm, v(1.26, 31.7) * mm, v(1.37, 31.4) * mm]});
            skFitSpline(sketch, "E230", {"points": [v(1.37, 31.4) * mm, v(1.5, 31.09) * mm, v(1.41, 29.92) * mm, v(1.2, 28.81) * mm]});
            skFitSpline(sketch, "E231", {"points": [v(1.2, 28.81) * mm, v(0.92, 27.44) * mm, v(0.9, 26.58) * mm, v(1.15, 26.13) * mm]});
            skFitSpline(sketch, "E232", {"points": [v(1.15, 26.13) * mm, v(1.7, 25.11) * mm, v(0.54, 18.94) * mm, v(-0.2, 18.94) * mm]});
            skFitSpline(sketch, "E233", {"points": [v(-0.2, 18.94) * mm, v(-0.36, 18.94) * mm, v(-0.71, 18.85) * mm, v(-0.99, 18.74) * mm]});
            skFitSpline(sketch, "E234", {"points": [v(-0.99, 18.74) * mm, v(-1.34, 18.61) * mm, v(-1.72, 19.06) * mm, v(-2.2, 20.19) * mm]});
            skFitSpline(sketch, "E235", {"points": [v(-5.19, 21.98) * mm, v(-7.25, 22.12) * mm, v(-7.68, 22.02) * mm, v(-9.82, 20.9) * mm]});
            skFitSpline(sketch, "E236", {"points": [v(-9.82, 20.9) * mm, v(-11.12, 20.23) * mm, v(-12.8, 19.49) * mm, v(-13.56, 19.26) * mm]});
            skFitSpline(sketch, "E237", {"points": [v(-13.56, 19.26) * mm, v(-14.8, 18.89) * mm, v(-15.02, 18.92) * mm, v(-15.75, 19.6) * mm]});
            skFitSpline(sketch, "E238", {"points": [v(-15.75, 19.6) * mm, v(-16.2, 20.03) * mm, v(-16.88, 20.32) * mm, v(-17.27, 20.27) * mm]});
            skFitSpline(sketch, "E239", {"points": [v(-17.27, 20.27) * mm, v(-17.74, 20.2) * mm, v(-18.15, 20.51) * mm, v(-18.52, 21.22) * mm]});
            skFitSpline(sketch, "E240", {"points": [v(-18.52, 21.22) * mm, v(-18.82, 21.79) * mm, v(-19.38, 22.53) * mm, v(-19.77, 22.86) * mm]});
            skFitSpline(sketch, "E241", {"points": [v(-19.77, 22.86) * mm, v(-20.4, 23.4) * mm, v(-20.47, 23.87) * mm, v(-20.43, 26.94) * mm]});
            skFitSpline(sketch, "E242", {"points": [v(-20.43, 26.94) * mm, v(-20.4, 30.15) * mm, v(-20.3, 30.6) * mm, v(-19.22, 32.7) * mm]});
            skFitSpline(sketch, "E243", {"points": [v(-19.22, 32.7) * mm, v(-18.58, 33.96) * mm, v(-17.68, 35.44) * mm, v(-17.23, 35.99) * mm]});
            skFitSpline(sketch, "E244", {"points": [v(-17.23, 35.99) * mm, v(-16.78, 36.54) * mm, v(-16.42, 37.15) * mm, v(-16.42, 37.36) * mm]});
            skFitSpline(sketch, "E245", {"points": [v(-16.42, 37.36) * mm, v(-16.42, 37.77) * mm, v(-14.75, 39.8) * mm, v(-12.1, 42.64) * mm]});
            skFitSpline(sketch, "E246", {"points": [v(-12.1, 42.64) * mm, v(-10.63, 44.21) * mm, v(-10.3, 44.4) * mm, v(-9.38, 44.22) * mm]});
            skFitSpline(sketch, "E247", {"points": [v(-9.38, 44.22) * mm, v(-8.8, 44.1) * mm, v(-8.24, 44.15) * mm, v(-8.13, 44.33) * mm]});
            skFitSpline(sketch, "E248", {"points": [v(-8.13, 44.33) * mm, v(-7.72, 45) * mm, v(-5.66, 45.75) * mm, v(-4.25, 45.75) * mm]});
            skFitSpline(sketch, "E249", {"points": [v(-4.25, 45.75) * mm, v(-3.27, 45.75) * mm, v(-2.49, 46) * mm, v(-1.95, 46.45) * mm]});
            skFitSpline(sketch, "E250", {"points": [v(-1.95, 46.45) * mm, v(-1.42, 46.92) * mm, v(-0.8, 47.15) * mm, v(-0.16, 47.16) * mm]});
            skLineSegment(sketch, "E251", {"start": v(-2.2, 20.19) * mm, "end": v(-2.91, 21.82) * mm});
            skLineSegment(sketch, "E252", {"start": v(-2.91, 21.82) * mm, "end": v(-5.19, 21.98) * mm});
            skLineSegment(sketch, "E253", {"start": v(-5.19, 21.98) * mm, "end": v(-2.2, 20.19) * mm});
            skFitSpline(sketch, "E254", {"points": [v(-4.72, 43.17) * mm, v(-4.85, 43.17) * mm, v(-4.97, 43.15) * mm, v(-5.08, 43.12) * mm]});
            skFitSpline(sketch, "E255", {"points": [v(-5.08, 43.12) * mm, v(-5.84, 42.88) * mm, v(-7, 41.16) * mm, v(-7.35, 39.71) * mm]});
            skFitSpline(sketch, "E256", {"points": [v(-7.35, 39.71) * mm, v(-7.48, 39.22) * mm, v(-8.14, 38.11) * mm, v(-8.82, 37.25) * mm]});
            skFitSpline(sketch, "E257", {"points": [v(-8.82, 37.25) * mm, v(-9.5, 36.4) * mm, v(-10.06, 35.58) * mm, v(-10.06, 35.45) * mm]});
            skFitSpline(sketch, "E258", {"points": [v(-10.06, 35.45) * mm, v(-10.07, 34.97) * mm, v(-12.28, 31.93) * mm, v(-12.76, 31.75) * mm]});
            skFitSpline(sketch, "E259", {"points": [v(-12.76, 31.75) * mm, v(-13.5, 31.46) * mm, v(-13.33, 30.6) * mm, v(-12.45, 30.23) * mm]});
            skFitSpline(sketch, "E260", {"points": [v(-12.45, 30.23) * mm, v(-11.84, 29.99) * mm, v(-9.74, 30.07) * mm, v(-9.5, 30.36) * mm]});
            skFitSpline(sketch, "E261", {"points": [v(-9.5, 30.36) * mm, v(-9.47, 30.38) * mm, v(-9.03, 31.09) * mm, v(-8.5, 31.93) * mm]});
            skFitSpline(sketch, "E262", {"points": [v(-8.5, 31.93) * mm, v(-7.54, 33.49) * mm, v(-6.65, 33.73) * mm, v(-6.8, 32.4) * mm]});
            skFitSpline(sketch, "E263", {"points": [v(-6.8, 32.4) * mm, v(-6.91, 31.37) * mm, v(-4.92, 30.37) * mm, v(-3.12, 30.54) * mm]});
            skFitSpline(sketch, "E264", {"points": [v(-3.12, 30.54) * mm, v(-2.44, 30.6) * mm, v(-0.96, 32.13) * mm, v(-0.57, 33.16) * mm]});
            skFitSpline(sketch, "E265", {"points": [v(-0.57, 33.16) * mm, v(0.08, 34.86) * mm, v(-0.87, 36.3) * mm, v(-2.92, 36.74) * mm]});
            skFitSpline(sketch, "E266", {"points": [v(-2.92, 36.74) * mm, v(-3.87, 36.94) * mm, v(-4.07, 37.15) * mm, v(-4.06, 37.93) * mm]});
            skFitSpline(sketch, "E267", {"points": [v(-4.06, 37.93) * mm, v(-4.05, 38.45) * mm, v(-3.66, 39.5) * mm, v(-3.18, 40.28) * mm]});
            skFitSpline(sketch, "E268", {"points": [v(-3.18, 40.28) * mm, v(-2.7, 41.06) * mm, v(-2.3, 41.87) * mm, v(-2.3, 42.1) * mm]});
            skFitSpline(sketch, "E269", {"points": [v(-2.3, 42.1) * mm, v(-2.3, 42.6) * mm, v(-3.79, 43.2) * mm, v(-4.72, 43.17) * mm]});
            skFitSpline(sketch, "E270", {"points": [v(0.31, 12.87) * mm, v(2.09, 12.97) * mm, v(3.16, 9.81) * mm, v(1.97, 7.7) * mm]});
            skFitSpline(sketch, "E271", {"points": [v(1.97, 7.7) * mm, v(1.37, 7.12) * mm, v(0.42, 7.17) * mm, v(-0.35, 7.08) * mm]});
            skFitSpline(sketch, "E272", {"points": [v(-0.35, 7.08) * mm, v(-4.1, 6.3) * mm, v(-3.05, 9.73) * mm, v(-1.64, 11.52) * mm]});
            skFitSpline(sketch, "E273", {"points": [v(-1.64, 11.52) * mm, v(-0.95, 12.44) * mm, v(-0.28, 12.84) * mm, v(0.31, 12.87) * mm]});
            skFitSpline(sketch, "E274", {"points": [v(-0.44, 1.2) * mm, v(2.39, 1.18) * mm, v(5.75, 0.65) * mm, v(4.18, -2.42) * mm]});
            skFitSpline(sketch, "E275", {"points": [v(4.18, -2.42) * mm, v(2.9, -4.1) * mm, v(0.21, -2.66) * mm, v(-1.58, -2.78) * mm]});
            skFitSpline(sketch, "E276", {"points": [v(-1.58, -2.78) * mm, v(-4.76, -3.95) * mm, v(-6.97, 1.52) * mm, v(-2.88, 1.11) * mm]});
            skFitSpline(sketch, "E277", {"points": [v(-2.88, 1.11) * mm, v(-2.26, 1.15) * mm, v(-1.38, 1.2) * mm, v(-0.44, 1.2) * mm]});
            skFitSpline(sketch, "E278", {"points": [v(-6.3, -9.46) * mm, v(-4.33, -9.47) * mm, v(-2.36, -10.85) * mm, v(-4.06, -13.07) * mm]});
            skFitSpline(sketch, "E279", {"points": [v(-4.06, -13.07) * mm, v(-4.7, -14.78) * mm, v(-9.69, -14.7) * mm, v(-9.18, -12.2) * mm]});
            skFitSpline(sketch, "E280", {"points": [v(-9.18, -12.2) * mm, v(-9.37, -10.3) * mm, v(-7.83, -9.46) * mm, v(-6.3, -9.46) * mm]});
            skFitSpline(sketch, "E281", {"points": [v(4.47, -10.16) * mm, v(5.54, -10.18) * mm, v(6.37, -10.55) * mm, v(5.85, -11.54) * mm]});
            skFitSpline(sketch, "E282", {"points": [v(5.85, -11.54) * mm, v(5.05, -12.1) * mm, v(3.99, -12.1) * mm, v(3.05, -12.09) * mm]});
            skFitSpline(sketch, "E283", {"points": [v(3.05, -12.09) * mm, v(-0.59, -11.37) * mm, v(2.4, -10.12) * mm, v(4.47, -10.16) * mm]});
            skFitSpline(sketch, "E284", {"points": [v(4.89, -16.75) * mm, v(5.34, -16.71) * mm, v(5.73, -17.09) * mm, v(5.67, -18.24) * mm]});
            skFitSpline(sketch, "E285", {"points": [v(4.86, -19.14) * mm, v(2.55, -18.91) * mm, v(3.88, -16.83) * mm, v(4.89, -16.75) * mm]});
            skLineSegment(sketch, "E286", {"start": v(5.67, -18.24) * mm, "end": v(5.36, -18.84) * mm});
            skLineSegment(sketch, "E287", {"start": v(5.36, -18.84) * mm, "end": v(4.86, -19.14) * mm});
            skLineSegment(sketch, "E288", {"start": v(4.86, -19.14) * mm, "end": v(5.67, -18.24) * mm});
            skFitSpline(sketch, "E289", {"points": [v(-8.8, -19.67) * mm, v(-8.31, -19.66) * mm, v(-7.97, -20.07) * mm, v(-8.41, -21.25) * mm]});
            skFitSpline(sketch, "E290", {"points": [v(-9.47, -21.63) * mm, v(-10.83, -20.87) * mm, v(-9.61, -19.68) * mm, v(-8.8, -19.67) * mm]});
            skLineSegment(sketch, "E291", {"start": v(-8.41, -21.25) * mm, "end": v(-8.88, -21.52) * mm});
            skLineSegment(sketch, "E292", {"start": v(-8.88, -21.52) * mm, "end": v(-9.47, -21.63) * mm});
            skLineSegment(sketch, "E293", {"start": v(-9.47, -21.63) * mm, "end": v(-8.41, -21.25) * mm});
            skSolve(sketch);
        }
        {
            var Q0;
            Q0 = qSketchRegion(id + "F2", true);
            var Q1;
            Q1=makeQuery(id+"F2.imprint","IMPRINT",FACE,{"disambiguationData":[TD([[makeQuery(id+"F2.imprint","IMPRINT",EDGE,{"derivedFrom":sQuery(id+"F2.wireOp",EDGE,"E254")}),1.0]])]});
            extrude(context, id + "F3", {"entities" : qUnion([Q0, Q1]), "operationType" : NewBodyOperationType.REMOVE, "oppositeDirection" : true, "depth" : 5 * mm});
        }
    });
